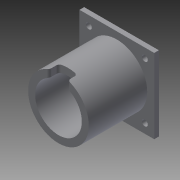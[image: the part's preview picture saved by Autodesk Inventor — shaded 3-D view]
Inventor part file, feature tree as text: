
AUTODESK INVENTOR PART (.ipt)
format: ipt  version: 2015 (Build 190159000, 159)  size: 151,040 bytes
history: native  units: in
note: dims shown in document units (in); Inventor stores cm internally (conversion verified against a paired STEP export)
features: sketch x5, extrude x4, hole x1, plane x1, fillet x1
ambient origin geometry x8: Origin, YZ Plane, XZ Plane, XY Plane, X Axis, Y Axis, Z Axis, Center Point
bodies: Solid1 (feature_tree)
feature tree (12):
  extrude  "Extrusion1"  Depth=1.6in
  extrude  "Extrusion2"  Depth=0.8in
  hole  "Hole1"  [1 undecoded]
  plane  "Work Plane1"
  extrude  "Extrusion3"  Depth=1.25in TaperAngle=0.0deg
  extrude  "Extrusion4"  Depth=0.05in
  fillet  "Fillet1"  Radius=0.2in
  sketch  "Sketch1"  dims[d0=1.6in d1=1.6in]
  sketch  "Sketch2"  dims[d2=0.8in d3=0.8in]
  sketch  "Sketch3"  dims[d4=0.1in d5=0.0in d6=1.0in]
  sketch  "Sketch4"  dims[d7=0.15in d8=1.25in d9=0.0in]
  sketch  "Sketch5"  dims[d10=0.2in d11=0.2in d12=0.2in d13=0.2in d14=0.2in d15=0.2in d16=0.2in d17=0.2in d18=0.125in d19=0.75in d20=0.375in d21=0.25in d22=0.5635in d23=0.125in d24=0.8108in d25=0.65in d26=0.2in d27=0.4in d28=0.2in d29=0.4in d30=0.0in d31=0.35in d32=0.4in d33=0.0in d34=0.05in]
note: 1 required parameter value undecoded (feature->parameter linkage not recoverable at this tier; creation-order binding heuristic only, values carry confidence <= 0.55)
